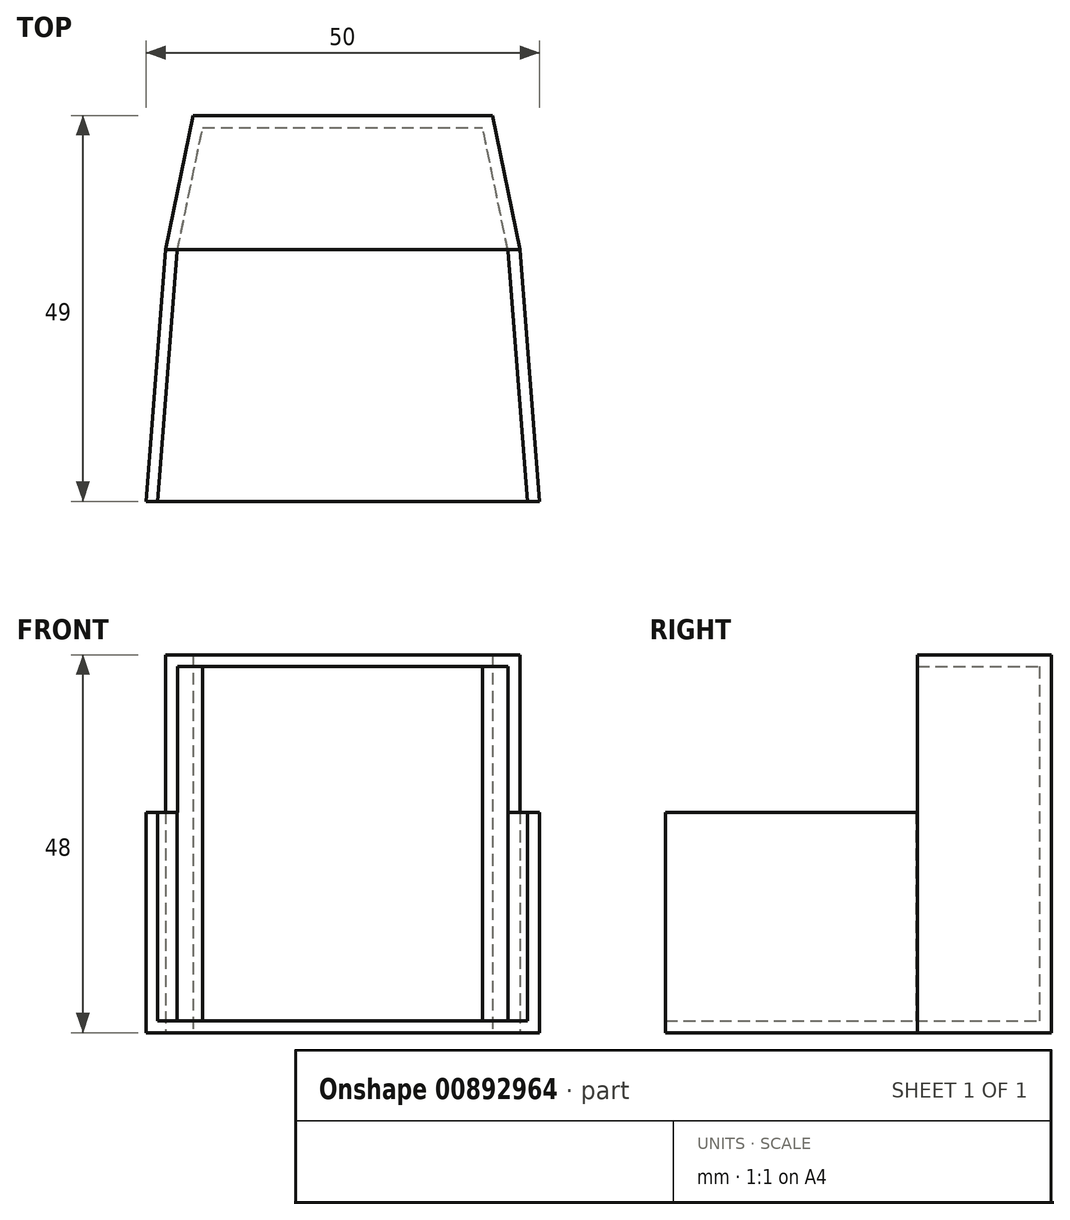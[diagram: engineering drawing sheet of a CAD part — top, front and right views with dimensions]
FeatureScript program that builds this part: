
annotation { "Feature Type Name" : "Feature", "Feature Type Description" : "" }
export const myFeature = defineFeature(function(context is Context, id is Id, definition is map)
    precondition{}
    {
        {
            var Q0;
            Q0=qCreatedBy(makeId("Top.planeOp"),FACE);
            var sketch = newSketch(context, id + "F0", { "sketchPlane" : qUnion([Q0])});
            skLineSegment(sketch, "E0", {"start": v(-19, 39.84) * mm, "end": v(19, 39.84) * mm});
            skLineSegment(sketch, "E1", {"start": v(25, -9.16) * mm, "end": v(-25, -9.16) * mm});
            skLineSegment(sketch, "E2", {"start": v(-22.5, 22.84) * mm, "end": v(22.5, 22.84) * mm});
            skLineSegment(sketch, "E3", {"start": v(-25, -9.16) * mm, "end": v(-22.5, 22.84) * mm});
            skLineSegment(sketch, "E4", {"start": v(25, -9.16) * mm, "end": v(22.5, 22.84) * mm});
            skLineSegment(sketch, "E5", {"start": v(-22.5, 22.84) * mm, "end": v(-19, 39.84) * mm});
            skLineSegment(sketch, "E6", {"start": v(22.5, 22.84) * mm, "end": v(19, 39.84) * mm});
            skSolve(sketch);
        }
        {
            var Q0;
            Q0=makeQuery(id+"F0.imprint","IMPRINT",FACE,{"disambiguationData":[TD([[makeQuery(id+"F0.imprint","IMPRINT",EDGE,{"derivedFrom":sQuery(id+"F0.wireOp",EDGE,"E1")}),-1.0]])]});
            var Q1;
            Q1=makeQuery(id+"F0.imprint","IMPRINT",FACE,{"disambiguationData":[TD([[makeQuery(id+"F0.imprint","IMPRINT",EDGE,{"derivedFrom":sQuery(id+"F0.wireOp",EDGE,"E0")}),-1.0]])]});
            extrude(context, id + "F1", {"entities" : qUnion([Q0, Q1]), "depth" : 48 * mm, "offsetDistance" : 25 * mm});
        }
        {
            var Q0;
            Q0=makeQuery(id+"F1.opExtrude","CAP_FACE",FACE,{"disambiguationData":[OSD([sQuery(id+"F0.wireOp",EDGE,"E0"),sQuery(id+"F0.wireOp",EDGE,"E1"),sQuery(id+"F0.wireOp",EDGE,"E3"),sQuery(id+"F0.wireOp",EDGE,"E4"),sQuery(id+"F0.wireOp",EDGE,"E5"),sQuery(id+"F0.wireOp",EDGE,"E6")])],"isStart":false});
            var sketch = newSketch(context, id + "F2", { "sketchPlane" : qUnion([Q0])});
            skLineSegment(sketch, "E7", {"start": v(-22.5, 22.84) * mm, "end": v(-19, 39.84) * mm});
            skLineSegment(sketch, "E8", {"start": v(-19, 39.84) * mm, "end": v(19, 39.84) * mm});
            skLineSegment(sketch, "E9", {"start": v(19, 39.84) * mm, "end": v(22.5, 22.84) * mm});
            skLineSegment(sketch, "E10", {"start": v(22.5, 22.84) * mm, "end": v(-22.5, 22.84) * mm});
            skLineSegment(sketch, "E11", {"start": v(-22.5, 22.84) * mm, "end": v(-25, -9.16) * mm});
            skLineSegment(sketch, "E12", {"start": v(-25, -9.16) * mm, "end": v(25, -9.16) * mm});
            skLineSegment(sketch, "E13", {"start": v(25, -9.16) * mm, "end": v(22.5, 22.84) * mm});
            skSolve(sketch);
        }
        {
            var Q0;
            Q0=makeQuery(id+"F2.imprint","IMPRINT",FACE,{"disambiguationData":[TD([[makeQuery(id+"F2.imprint","IMPRINT",EDGE,{"derivedFrom":sQuery(id+"F2.wireOp",EDGE,"E10")}),1.0]])]});
            extrude(context, id + "F3", {"entities" : qUnion([Q0]), "operationType" : NewBodyOperationType.REMOVE, "oppositeDirection" : true, "depth" : 20 * mm, "offsetDistance" : 25 * mm});
        }
        {
            var Q0;
            Q0=makeQuery(id+"F3.boolean.opBoolean","COPY",FACE,{"derivedFrom":makeQuery(id+"F3.opExtrude","SWEPT_FACE",FACE,{"disambiguationData":[OSD([sQuery(id+"F2.wireOp",EDGE,"E10")])]})});
            var Q1;
            Q1=makeQuery(id+"F3.boolean.opBoolean","COPY",FACE,{"derivedFrom":makeQuery(id+"F3.opExtrude","CAP_FACE",FACE,{"disambiguationData":[OSD([sQuery(id+"F2.wireOp",EDGE,"E10"),sQuery(id+"F2.wireOp",EDGE,"E11"),sQuery(id+"F2.wireOp",EDGE,"E12"),sQuery(id+"F2.wireOp",EDGE,"E13")])],"isStart":false})});
            var Q2;
            Q2=makeQuery(id+"F1.opExtrude","SWEPT_FACE",FACE,{"disambiguationData":[OSD([sQuery(id+"F0.wireOp",EDGE,"E1")])]});
            shell(context, id + "F4", {"entities" : qUnion([Q0, Q1, Q2]), "thickness" : 1.5 * mm});
        }
    });
